# Revit family: Power-ModularDevices-GEWISS-90AM-SWITCH_DISCONNECTOR_2P
name_source: partatom
category: Apparecchi elettrici
revit_build: Autodesk Revit 2016 (Build: 20161004_0715(x64)
units: mm (PartAtom-declared; Revit-internal decimal feet)

## family parameters
Condiviso = No
Host = Superficie
Mantenere orientamento annotazione = Sì
Numero OmniClass = 23.80.50.00
Punto di calcolo locali = Sì
Quota connettore circolare = Usa diametro
Taglio con vuoti quando caricato = No
Tipo di parte = Normale
Titolo OmniClass = Terminals for Power Supply

## types (6) — shared parameters
Catalogue = POWER
Catalogue Range = 90 AM
Electrocod = 1422
IDF = 01abd0a7-65c1-45c8-9aa0-f9a4f1632530
IDT = 2c0e4de9-973c-44a3-b66b-2ab3e92ec152
Immagine tipo = GW96114.jpg
No. Chorus modules = 2
No. of modules EN 50022 = 2
No. of poles = 2P
Number of poles = 2P
Numero di poli = 1
Produttore = GEWISS S.p.A.
Prospetto di default = 1219 mm
Rated voltage AC = 415V
SEO = Disconnector
Spostamento_x = -340 mm
Standard = EN 60947-3
Technical sheet = https://www.gewiss.com
URL = https://www.gewiss.com
Version file RFA = 18.0
carico = Altro
potenza in watt = 0 V

## per-type parameters (varying)
| type | Descrizione | EAN code | Modello | Rated current (In) | Rated current: | Rated voltage |
| GW96158 - SWITCH DISCONNECTOR 2P 100A | SWITCH DISCONNECTOR 2P 100A | 8011564131675 | GW96158 | 100A | 100A | 415V |
| GW96157 - SWITCH DISCONNECTOR 2P 80A | SWITCH DISCONNECTOR 2P 80A | 8011564131668 | GW96157 | 80A | 80A | 415Vac |
| GW96114 - SWITCH DISCONNECTOR 2P 32A | SWITCH DISCONNECTOR 2P 32A | 8011564110298 | GW96114 | 32A | 32A | 415Vac |
| GW96115 - SWITCH DISCONNECTOR 2P 40A | SWITCH DISCONNECTOR 2P 40A | 8011564110304 | GW96115 | 40A | 40A | 415Vac |
| GW96156 - SWITCH DISCONNECTOR 2P 63A | SWITCH DISCONNECTOR 2P 63A | 8011564131651 | GW96156 | 63A | 63A | 415V |
| GW96159 - SWITCH DISCONNECTOR 2P 125A | SWITCH DISCONNECTOR 2P 125A | 8011564131682 | GW96159 | 125A | 125A | 415Vac |
